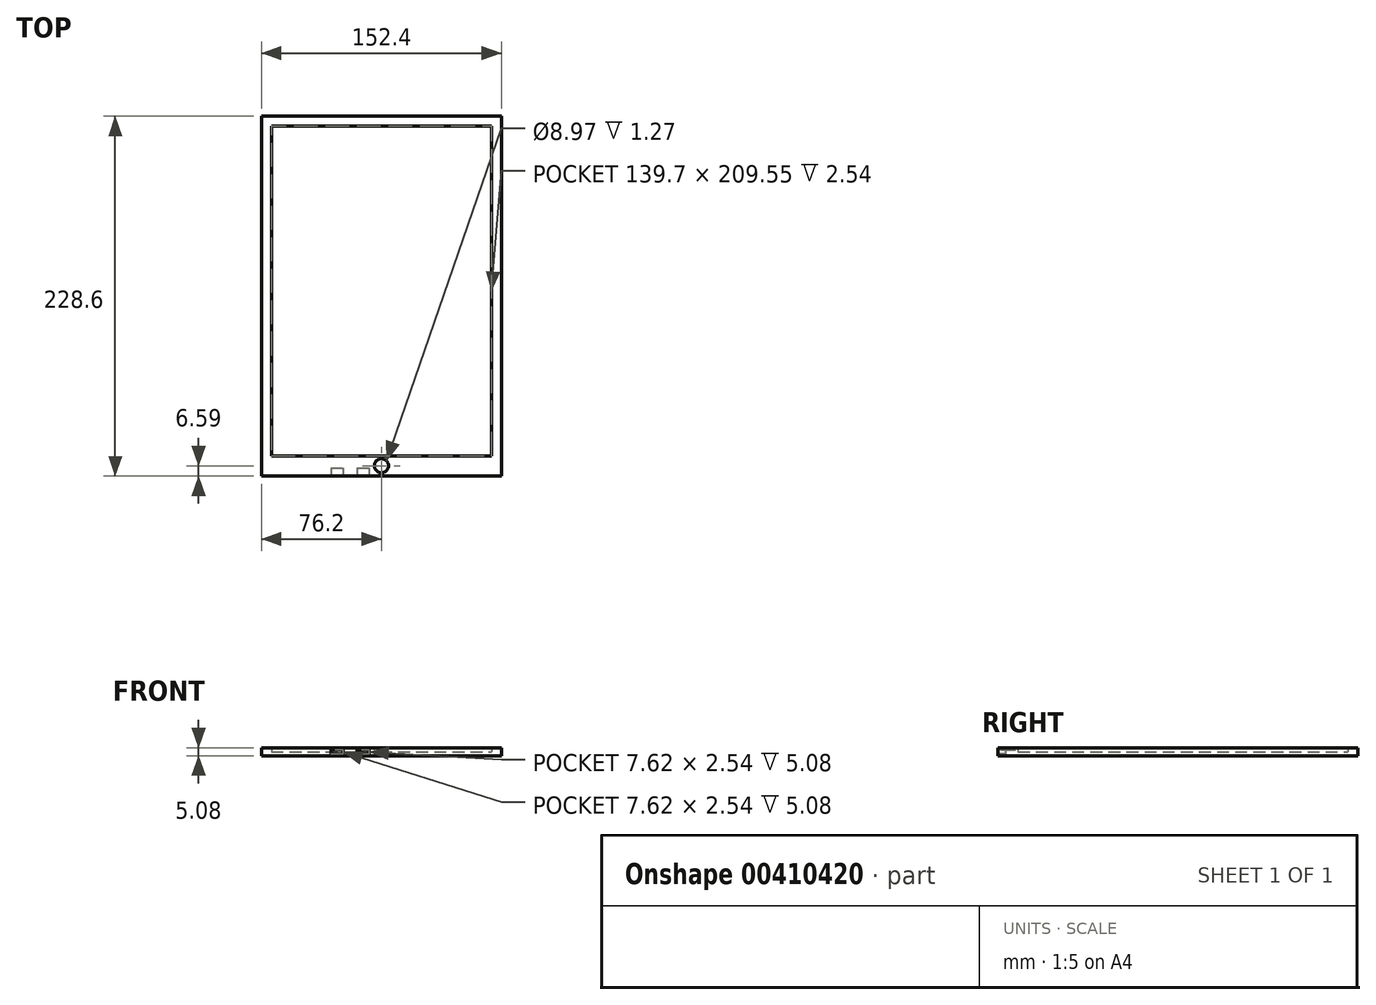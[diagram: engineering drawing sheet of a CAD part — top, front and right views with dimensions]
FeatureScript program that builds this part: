
annotation { "Feature Type Name" : "Feature", "Feature Type Description" : "" }
export const myFeature = defineFeature(function(context is Context, id is Id, definition is map)
    precondition{}
    {
        {
            var Q0;
            Q0=qCreatedBy(makeId("Top.planeOp"),FACE);
            var sketch = newSketch(context, id + "F0", { "sketchPlane" : qUnion([Q0])});
            skLineSegment(sketch, "E0.bottom", {"start": v(-76.2, 114.3) * mm, "end": v(76.2, 114.3) * mm});
            skLineSegment(sketch, "E0.top", {"start": v(-76.2, -114.3) * mm, "end": v(76.2, -114.3) * mm});
            skLineSegment(sketch, "E0.left", {"start": v(-76.2, 114.3) * mm, "end": v(-76.2, -114.3) * mm});
            skLineSegment(sketch, "E0.right", {"start": v(76.2, 114.3) * mm, "end": v(76.2, -114.3) * mm});
            skPoint(sketch, "E0.middle", {"position": v(0, 0) * mm});
            skLineSegment(sketch, "E1.top", {"start": v(-69.85, -101.6) * mm, "end": v(69.85, -101.6) * mm});
            skLineSegment(sketch, "E1.left", {"start": v(-69.85, 101.6) * mm, "end": v(-69.85, -101.6) * mm});
            skLineSegment(sketch, "E1.right", {"start": v(69.85, 101.6) * mm, "end": v(69.85, -101.6) * mm});
            skLineSegment(sketch, "E2.top", {"start": v(-69.85, 107.95) * mm, "end": v(69.85, 107.95) * mm});
            skLineSegment(sketch, "E2.left", {"start": v(-69.85, 101.6) * mm, "end": v(-69.85, 107.95) * mm});
            skLineSegment(sketch, "E2.right", {"start": v(69.85, 101.6) * mm, "end": v(69.85, 107.95) * mm});
            skSolve(sketch);
        }
        {
            var Q0;
            Q0=makeQuery(id+"F0.imprint","IMPRINT",FACE,{"disambiguationData":[TD([[makeQuery(id+"F0.imprint","IMPRINT",EDGE,{"derivedFrom":sQuery(id+"F0.wireOp",EDGE,"E0.bottom")}),-1.0]])]});
            extrude(context, id + "F1", {"entities" : qUnion([Q0]), "depth" : 5.08 * mm});
        }
        {
            var Q0;
            Q0=makeQuery(id+"F0.imprint","IMPRINT",FACE,{"disambiguationData":[TD([[makeQuery(id+"F0.imprint","IMPRINT",EDGE,{"derivedFrom":sQuery(id+"F0.wireOp",EDGE,"E1.top")}),1.0]])]});
            extrude(context, id + "F2", {"entities" : qUnion([Q0]), "operationType" : NewBodyOperationType.ADD, "depth" : 2.54 * mm});
        }
        {
            var Q0;
            Q0=makeQuery(id+"F1.opExtrude","CAP_FACE",FACE,{"disambiguationData":[OSD([sQuery(id+"F0.wireOp",EDGE,"E0.bottom"),sQuery(id+"F0.wireOp",EDGE,"E0.top"),sQuery(id+"F0.wireOp",EDGE,"E0.left"),sQuery(id+"F0.wireOp",EDGE,"E0.right"),sQuery(id+"F0.wireOp",EDGE,"E1.top"),sQuery(id+"F0.wireOp",EDGE,"E1.left"),sQuery(id+"F0.wireOp",EDGE,"E1.right"),sQuery(id+"F0.wireOp",EDGE,"E2.top"),sQuery(id+"F0.wireOp",EDGE,"E2.left"),sQuery(id+"F0.wireOp",EDGE,"E2.right")])],"isStart":false});
            var sketch = newSketch(context, id + "F3", { "sketchPlane" : qUnion([Q0])});
            skCircle(sketch, "E3", {"center": v(0, -107.71) * mm, "radius": 4.49 * mm});
            skPoint(sketch, "E3.centerSnap0", {"position": v(0, -101.6) * mm});
            skSolve(sketch);
        }
        {
            var Q0;
            Q0 = qSketchRegion(id + "F3", true);
            extrude(context, id + "F4", {"entities" : qUnion([Q0]), "operationType" : NewBodyOperationType.REMOVE, "oppositeDirection" : true, "depth" : 1.27 * mm});
        }
        {
            var Q0;
            Q0=makeQuery(id+"F1.opExtrude","SWEPT_FACE",FACE,{"disambiguationData":[OSD([sQuery(id+"F0.wireOp",EDGE,"E0.top")])]});
            var sketch = newSketch(context, id + "F5", { "sketchPlane" : qUnion([Q0])});
            skLineSegment(sketch, "E4.bottom", {"start": v(-32.07, 1.02) * mm, "end": v(-24.45, 1.02) * mm});
            skLineSegment(sketch, "E4.top", {"start": v(-32.07, 3.56) * mm, "end": v(-24.45, 3.56) * mm});
            skLineSegment(sketch, "E4.left", {"start": v(-32.07, 1.02) * mm, "end": v(-32.07, 3.56) * mm});
            skLineSegment(sketch, "E4.right", {"start": v(-24.45, 1.02) * mm, "end": v(-24.45, 3.56) * mm});
            skLineSegment(sketch, "E5.bottom", {"start": v(-15.49, 1.02) * mm, "end": v(-7.87, 1.02) * mm});
            skLineSegment(sketch, "E5.top", {"start": v(-15.49, 3.56) * mm, "end": v(-7.87, 3.56) * mm});
            skLineSegment(sketch, "E5.left", {"start": v(-15.49, 1.02) * mm, "end": v(-15.49, 3.56) * mm});
            skLineSegment(sketch, "E5.right", {"start": v(-7.87, 1.02) * mm, "end": v(-7.87, 3.56) * mm});
            skSolve(sketch);
        }
        {
            var Q0;
            Q0 = qSketchRegion(id + "F5", true);
            extrude(context, id + "F6", {"entities" : qUnion([Q0]), "operationType" : NewBodyOperationType.REMOVE, "oppositeDirection" : true, "depth" : 5.08 * mm});
        }
    });
